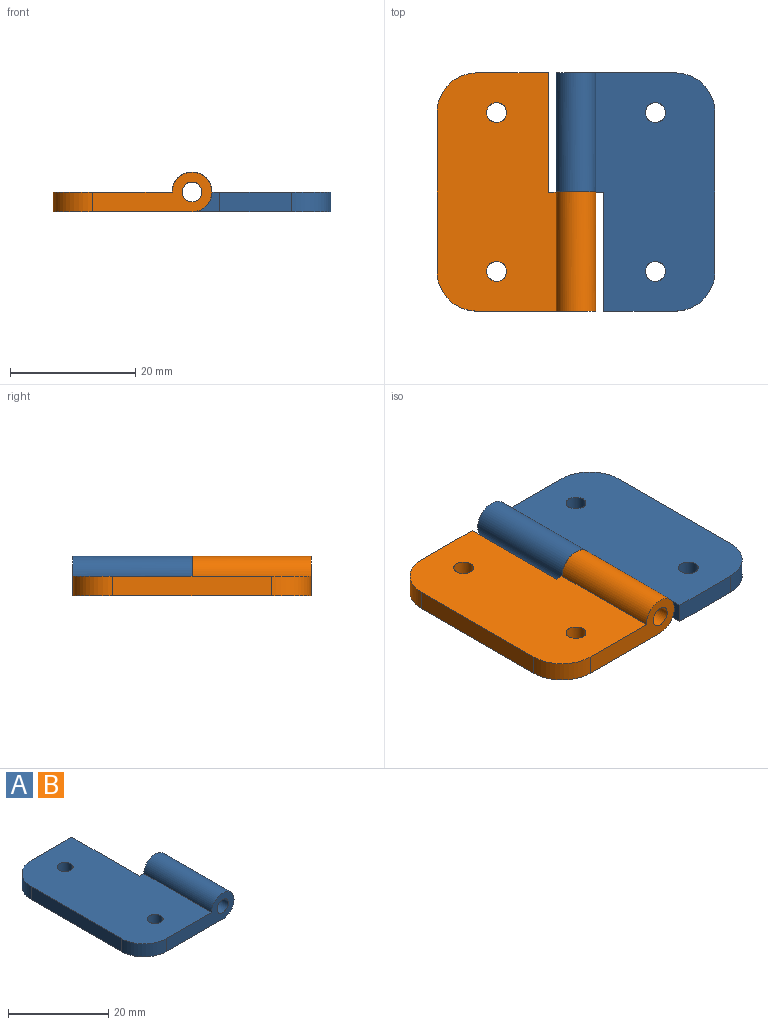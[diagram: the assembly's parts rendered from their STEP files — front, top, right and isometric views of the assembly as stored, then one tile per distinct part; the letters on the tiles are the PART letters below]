
ASSEMBLY  parts=2 mates=1
PART A: 13 faces, bbox 25.4x38.1x6.4 mm
  f0: cylinder r=3.17mm len=19.05mm, axis (0,-1,0), area 285mm2, adj f3,f4,f8,f10
  f1: cylinder r=1.59mm len=19.05mm, axis (0,-1,0), area 190mm2, adj f3,f10
  f2: plane 11.43x3.18mm, normal (0,1,0), area 36.3mm2, adj f4,f5,f8,f9
  f3: plane 19.05x6.35mm, normal (0,-1,0), area 66.2mm2, adj f0,f1,f4,f7,f8
  f4: plane 38.1x22.23mm, normal (0,0,-1), area 729mm2, adj f0,f2,f3,f5,f6,f7,f9,f10
  f5: cylinder r=6.35mm len=6.35mm, axis (0,0,-1), area 31.7mm2, adj f2,f4,f6,f8
  f6: plane 25.4x3.18mm, normal (-1,0,0), area 80.6mm2, adj f4,f5,f7,f8
  f7: cylinder r=6.35mm len=6.35mm, axis (0,0,-1), area 31.7mm2, adj f3,f4,f6,f8
  f8: plane 38.1x19.05mm, normal (0,0,1), area 668.5mm2, adj f0,f2,f3,f5,f6,f7,f9,f10
  f9: plane 19.05x3.18mm, normal (1,0,0), area 60.5mm2, adj f2,f4,f8,f10
  f10: plane 7.62x6.35mm, normal (0,1,0), area 29.9mm2, adj f0,f1,f4,f8,f9
  f11: cylinder r=1.59mm len=3.18mm, axis (0,0,-1), area 31.7mm2, adj f4,f8
  f12: cylinder r=1.59mm len=3.18mm, axis (0,0,-1), area 31.7mm2, adj f4,f8
PART B: same geometry as A
PLACE A rot(axis=(0,0,1),180deg) t=(-5.7,-3.39,2.76)mm fixed
PLACE B t=(-24.75,-3.39,2.76)mm
MATE revolute B.f0 <-> A.f0  axis (0,1,0) through (-15.23,-3.39,5.94)mm
